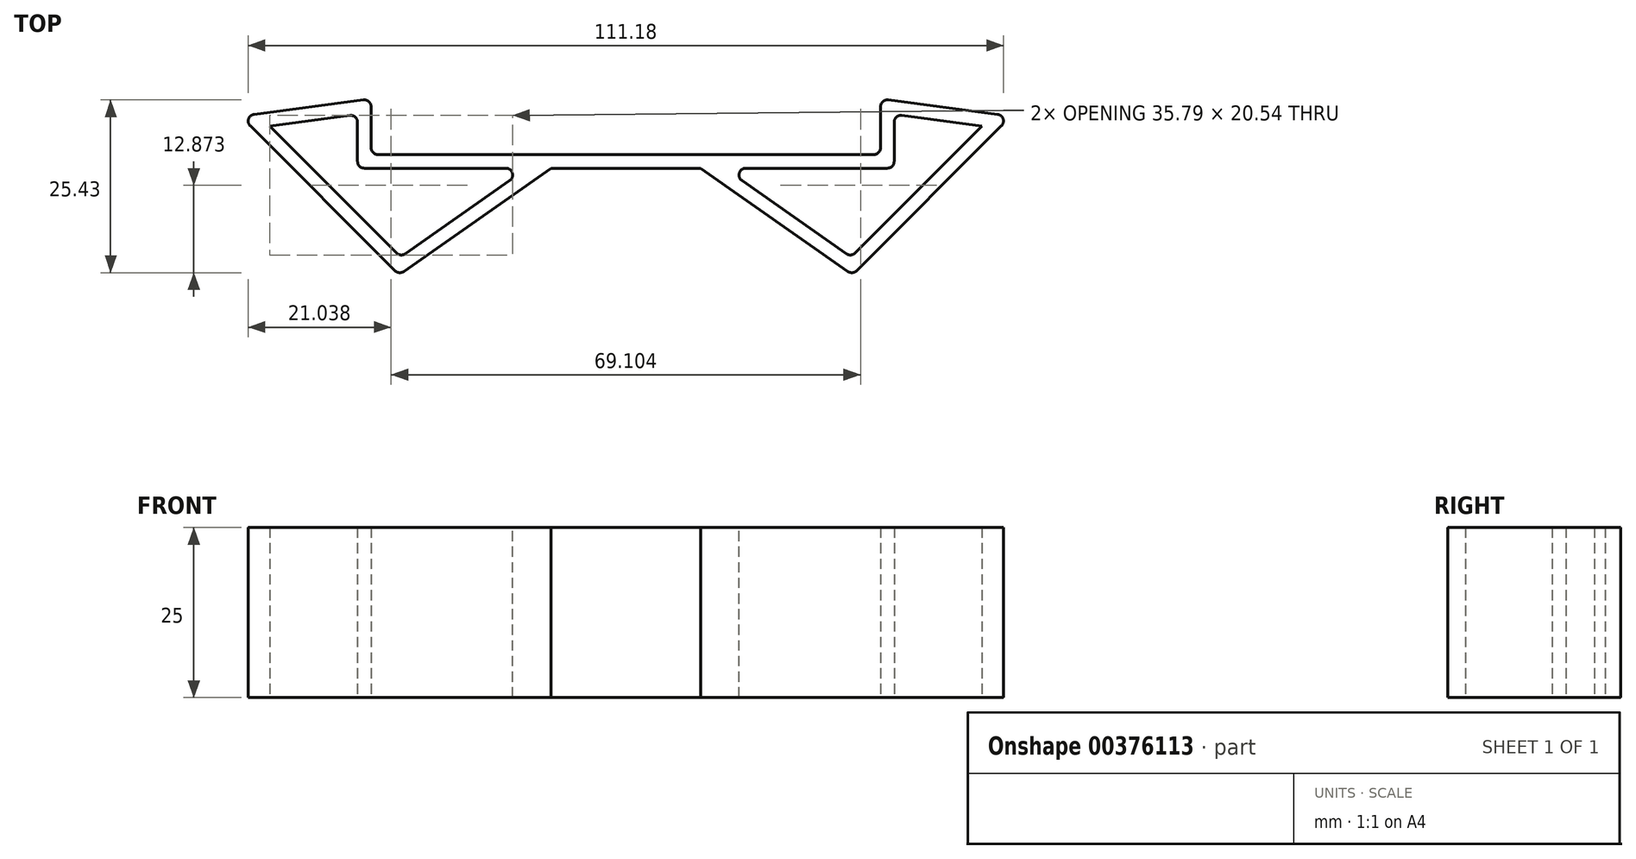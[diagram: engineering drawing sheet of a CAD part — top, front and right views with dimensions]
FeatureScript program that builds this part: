
annotation { "Feature Type Name" : "Feature", "Feature Type Description" : "" }
export const myFeature = defineFeature(function(context is Context, id is Id, definition is map)
    precondition{}
    {
        {
            var Q0;
            Q0=qCreatedBy(makeId("Top.planeOp"),FACE);
            var sketch = newSketch(context, id + "F0", { "sketchPlane" : qUnion([Q0])});
            skLineSegment(sketch, "E0", {"start": v(0, 0) * mm, "end": v(-37.5, 0) * mm});
            skLineSegment(sketch, "E1", {"start": v(-37.5, 0) * mm, "end": v(-37.5, 8.2) * mm});
            skLineSegment(sketch, "E2", {"start": v(-37.5, 8.2) * mm, "end": v(-56.73, 5.67) * mm});
            skLineSegment(sketch, "E3", {"start": v(-56.73, 5.67) * mm, "end": v(-33.38, -17.67) * mm});
            skLineSegment(sketch, "E4", {"start": v(-33.38, -17.67) * mm, "end": v(-11, -2) * mm});
            skLineSegment(sketch, "E5", {"start": v(-11, -2) * mm, "end": v(0, -2) * mm});
            skLineSegment(sketch, "E6", {"start": v(0, 14.81) * mm, "end": v(0, -16.78) * mm});
            skLineSegment(sketch, "E7.0", {"start": v(-39.5, -2) * mm, "end": v(-39.5, 5.92) * mm});
            skLineSegment(sketch, "E7.1", {"start": v(0, -2) * mm, "end": v(-39.5, -2) * mm});
            skLineSegment(sketch, "E8.0", {"start": v(-33.16, -15.07) * mm, "end": v(-14.49, -2) * mm});
            skLineSegment(sketch, "E9.MirrorCS", {"start": v(37.5, 0) * mm, "end": v(37.5, 8.2) * mm});
            skLineSegment(sketch, "E10.MirrorCS", {"start": v(37.5, 8.2) * mm, "end": v(56.73, 5.67) * mm});
            skLineSegment(sketch, "E11.MirrorCS", {"start": v(56.73, 5.67) * mm, "end": v(33.38, -17.67) * mm});
            skLineSegment(sketch, "E12.MirrorCS", {"start": v(33.38, -17.67) * mm, "end": v(11, -2) * mm});
            skLineSegment(sketch, "E13.MirrorCS", {"start": v(33.16, -15.07) * mm, "end": v(14.49, -2) * mm});
            skLineSegment(sketch, "E14.MirrorCS", {"start": v(39.5, -2) * mm, "end": v(39.5, 5.92) * mm});
            skLineSegment(sketch, "E15.MirrorCS", {"start": v(0, -2) * mm, "end": v(39.5, -2) * mm});
            skLineSegment(sketch, "E16.MirrorCS", {"start": v(11, -2) * mm, "end": v(0, -2) * mm});
            skLineSegment(sketch, "E17.MirrorCS", {"start": v(0, 0) * mm, "end": v(37.5, 0) * mm});
            skPoint(sketch, "E18", {"position": v(-19.75, -2) * mm});
            skLineSegment(sketch, "E19", {"start": v(-33.16, -15.07) * mm, "end": v(-52.45, 4.22) * mm});
            skLineSegment(sketch, "E20", {"start": v(-52.45, 4.22) * mm, "end": v(-39.5, 5.92) * mm});
            skLineSegment(sketch, "E21.MirrorCS", {"start": v(33.16, -15.07) * mm, "end": v(52.45, 4.22) * mm});
            skLineSegment(sketch, "E22.MirrorCS", {"start": v(52.45, 4.22) * mm, "end": v(39.5, 5.92) * mm});
            skSolve(sketch);
        }
        {
            var Q0;
            {var subQ6=sQuery(id+"F0.wireOp",EDGE,"E3");Q0=makeQuery(id+"F0.imprint","IMPRINT",FACE,{"disambiguationData":[TD([[makeQuery(id+"F0.imprint","IMPRINT",EDGE,{"derivedFrom":subQ6}),1.0]])]});}
            var Q1;
            {var subQ0=sQuery(id+"F0.wireOp",EDGE,"E2");var subQ1=sQuery(id+"F0.wireOp",EDGE,"E1");var subQ2=makeQuery(id+"F0.imprint","INTERSECT",VERTEX,{"derivedFrom":[subQ1,subQ0]});Q1=makeQuery(id+"F0.imprint","IMPRINT",FACE,{"disambiguationData":[TD([[makeQuery(id+"F0.imprint","IMPRINT",EDGE,{"disambiguationData":[TD([[subQ2,1.0]])],"derivedFrom":subQ1}),1.0]])]});}
            var Q2;
            {var subQ1=sQuery(id+"F0.wireOp",EDGE,"E0");Q2=makeQuery(id+"F0.imprint","IMPRINT",FACE,{"disambiguationData":[TD([[makeQuery(id+"F0.imprint","IMPRINT",EDGE,{"derivedFrom":subQ1}),1.0]])]});}
            var Q3;
            {var subQ0=sQuery(id+"F0.wireOp",EDGE,"E11.MirrorCS");Q3=makeQuery(id+"F0.imprint","IMPRINT",FACE,{"disambiguationData":[TD([[makeQuery(id+"F0.imprint","IMPRINT",EDGE,{"derivedFrom":subQ0}),-1.0]])]});}
            var Q4;
            {var subQ7=sQuery(id+"F0.wireOp",EDGE,"E17.MirrorCS");Q4=makeQuery(id+"F0.imprint","IMPRINT",FACE,{"disambiguationData":[TD([[makeQuery(id+"F0.imprint","IMPRINT",EDGE,{"derivedFrom":subQ7}),-1.0]])]});}
            var Q5;
            {var subQ0=sQuery(id+"F0.wireOp",EDGE,"E10.MirrorCS");var subQ1=sQuery(id+"F0.wireOp",EDGE,"E9.MirrorCS");var subQ2=makeQuery(id+"F0.imprint","INTERSECT",VERTEX,{"derivedFrom":[subQ1,subQ0]});Q5=makeQuery(id+"F0.imprint","IMPRINT",FACE,{"disambiguationData":[TD([[makeQuery(id+"F0.imprint","IMPRINT",EDGE,{"disambiguationData":[TD([[subQ2,1.0]])],"derivedFrom":subQ1}),-1.0]])]});}
            var Q6;
            {var subQ0=sQuery(id+"F0.wireOp",EDGE,"E7.0");var subQ1=sQuery(id+"F0.wireOp",EDGE,"12d51f8c-d412-4ac5-94a4-2e461e6358c8.0");var subQ2=makeQuery(id+"F0.imprint","INTERSECT",VERTEX,{"derivedFrom":[subQ1,subQ0]});Q6=makeQuery(id+"F0.imprint","IMPRINT",FACE,{"disambiguationData":[TD([[makeQuery(id+"F0.imprint","IMPRINT",EDGE,{"disambiguationData":[TD([[subQ2,-1.0]])],"derivedFrom":subQ1}),-1.0]])]});}
            extrude(context, id + "F1", {"entities" : qUnion([Q0, Q1, Q2, Q3, Q4, Q5, Q6]), "depth" : 25 * mm});
        }
        {
            var Q0;
            Q0=makeQuery(id+"F1.opExtrude","SWEPT_EDGE",EDGE,{"disambiguationData":[OSD([sQuery(id+"F0.wireOp",EDGE,"E1"),sQuery(id+"F0.wireOp",EDGE,"E2")])]});
            var Q1;
            Q1=makeQuery(id+"F1.opExtrude","SWEPT_EDGE",EDGE,{"disambiguationData":[OSD([sQuery(id+"F0.wireOp",EDGE,"E2"),sQuery(id+"F0.wireOp",EDGE,"E3")])]});
            var Q2;
            Q2=makeQuery(id+"F1.opExtrude","SWEPT_EDGE",EDGE,{"disambiguationData":[OSD([sQuery(id+"F0.wireOp",EDGE,"E3"),sQuery(id+"F0.wireOp",EDGE,"E4")])]});
            var Q3;
            Q3=makeQuery(id+"F1.opExtrude","SWEPT_EDGE",EDGE,{"disambiguationData":[OSD([sQuery(id+"F0.wireOp",EDGE,"E0"),sQuery(id+"F0.wireOp",EDGE,"E1")])]});
            var Q4;
            Q4=makeQuery(id+"F1.opExtrude","SWEPT_EDGE",EDGE,{"disambiguationData":[OSD([sQuery(id+"F0.wireOp",EDGE,"E7.0"),sQuery(id+"F0.wireOp",EDGE,"E7.1")])]});
            var Q5;
            Q5=makeQuery(id+"F1.opExtrude","SWEPT_EDGE",EDGE,{"disambiguationData":[OSD([sQuery(id+"F0.wireOp",EDGE,"E9.MirrorCS"),sQuery(id+"F0.wireOp",EDGE,"E17.MirrorCS")])]});
            var Q6;
            Q6=makeQuery(id+"F1.opExtrude","SWEPT_EDGE",EDGE,{"disambiguationData":[OSD([sQuery(id+"F0.wireOp",EDGE,"E9.MirrorCS"),sQuery(id+"F0.wireOp",EDGE,"E10.MirrorCS")])]});
            var Q7;
            Q7=makeQuery(id+"F1.opExtrude","SWEPT_EDGE",EDGE,{"disambiguationData":[OSD([sQuery(id+"F0.wireOp",EDGE,"E10.MirrorCS"),sQuery(id+"F0.wireOp",EDGE,"E11.MirrorCS")])]});
            var Q8;
            Q8=makeQuery(id+"F1.opExtrude","SWEPT_EDGE",EDGE,{"disambiguationData":[OSD([sQuery(id+"F0.wireOp",EDGE,"E14.MirrorCS"),sQuery(id+"F0.wireOp",EDGE,"E15.MirrorCS")])]});
            var Q9;
            Q9=makeQuery(id+"F1.opExtrude","SWEPT_EDGE",EDGE,{"disambiguationData":[OSD([sQuery(id+"F0.wireOp",EDGE,"E11.MirrorCS"),sQuery(id+"F0.wireOp",EDGE,"E12.MirrorCS")])]});
            var Q10;
            Q10=makeQuery(id+"F1.opExtrude","SWEPT_EDGE",EDGE,{"disambiguationData":[OSD([sQuery(id+"F0.wireOp",EDGE,"E13.MirrorCS"),sQuery(id+"F0.wireOp",EDGE,"16f77f33-1f45-4862-819a-b43949d90e557.MirrorCS")])]});
            var Q11;
            Q11=makeQuery(id+"F1.opExtrude","SWEPT_EDGE",EDGE,{"disambiguationData":[OSD([sQuery(id+"F0.wireOp",EDGE,"E13.MirrorCS"),sQuery(id+"F0.wireOp",EDGE,"E15.MirrorCS")])]});
            var Q12;
            Q12=makeQuery(id+"F1.opExtrude","SWEPT_EDGE",EDGE,{"disambiguationData":[OSD([sQuery(id+"F0.wireOp",EDGE,"E14.MirrorCS"),sQuery(id+"F0.wireOp",EDGE,"16f77f33-1f45-4862-819a-b43949d90e556.MirrorCS")])]});
            var Q13;
            Q13=makeQuery(id+"F1.opExtrude","SWEPT_EDGE",EDGE,{"disambiguationData":[OSD([sQuery(id+"F0.wireOp",EDGE,"16f77f33-1f45-4862-819a-b43949d90e556.MirrorCS"),sQuery(id+"F0.wireOp",EDGE,"16f77f33-1f45-4862-819a-b43949d90e557.MirrorCS")])]});
            var Q14;
            Q14=makeQuery(id+"F1.opExtrude","SWEPT_EDGE",EDGE,{"disambiguationData":[OSD([sQuery(id+"F0.wireOp",EDGE,"12d51f8c-d412-4ac5-94a4-2e461e6358c8.0"),sQuery(id+"F0.wireOp",EDGE,"12d51f8c-d412-4ac5-94a4-2e461e6358c8.1")])]});
            var Q15;
            Q15=makeQuery(id+"F1.opExtrude","SWEPT_EDGE",EDGE,{"disambiguationData":[OSD([sQuery(id+"F0.wireOp",EDGE,"12d51f8c-d412-4ac5-94a4-2e461e6358c8.1"),sQuery(id+"F0.wireOp",EDGE,"E7.0")])]});
            var Q16;
            Q16=makeQuery(id+"F1.opExtrude","SWEPT_EDGE",EDGE,{"disambiguationData":[OSD([sQuery(id+"F0.wireOp",EDGE,"12d51f8c-d412-4ac5-94a4-2e461e6358c8.0"),sQuery(id+"F0.wireOp",EDGE,"E8.0")])]});
            var Q17;
            Q17=makeQuery(id+"F1.opExtrude","SWEPT_EDGE",EDGE,{"disambiguationData":[OSD([sQuery(id+"F0.wireOp",EDGE,"E7.1"),sQuery(id+"F0.wireOp",EDGE,"E8.0")])]});
            fillet(context, id + "F2", {"entities" : qUnion([Q0, Q1, Q2, Q3, Q4, Q5, Q6, Q7, Q8, Q9, Q10, Q11, Q12, Q13, Q14, Q15, Q16, Q17]), "radius" : 1 * mm, "tangentPropagation" : true, "allowEdgeOverflow" : false});
        }
    });
